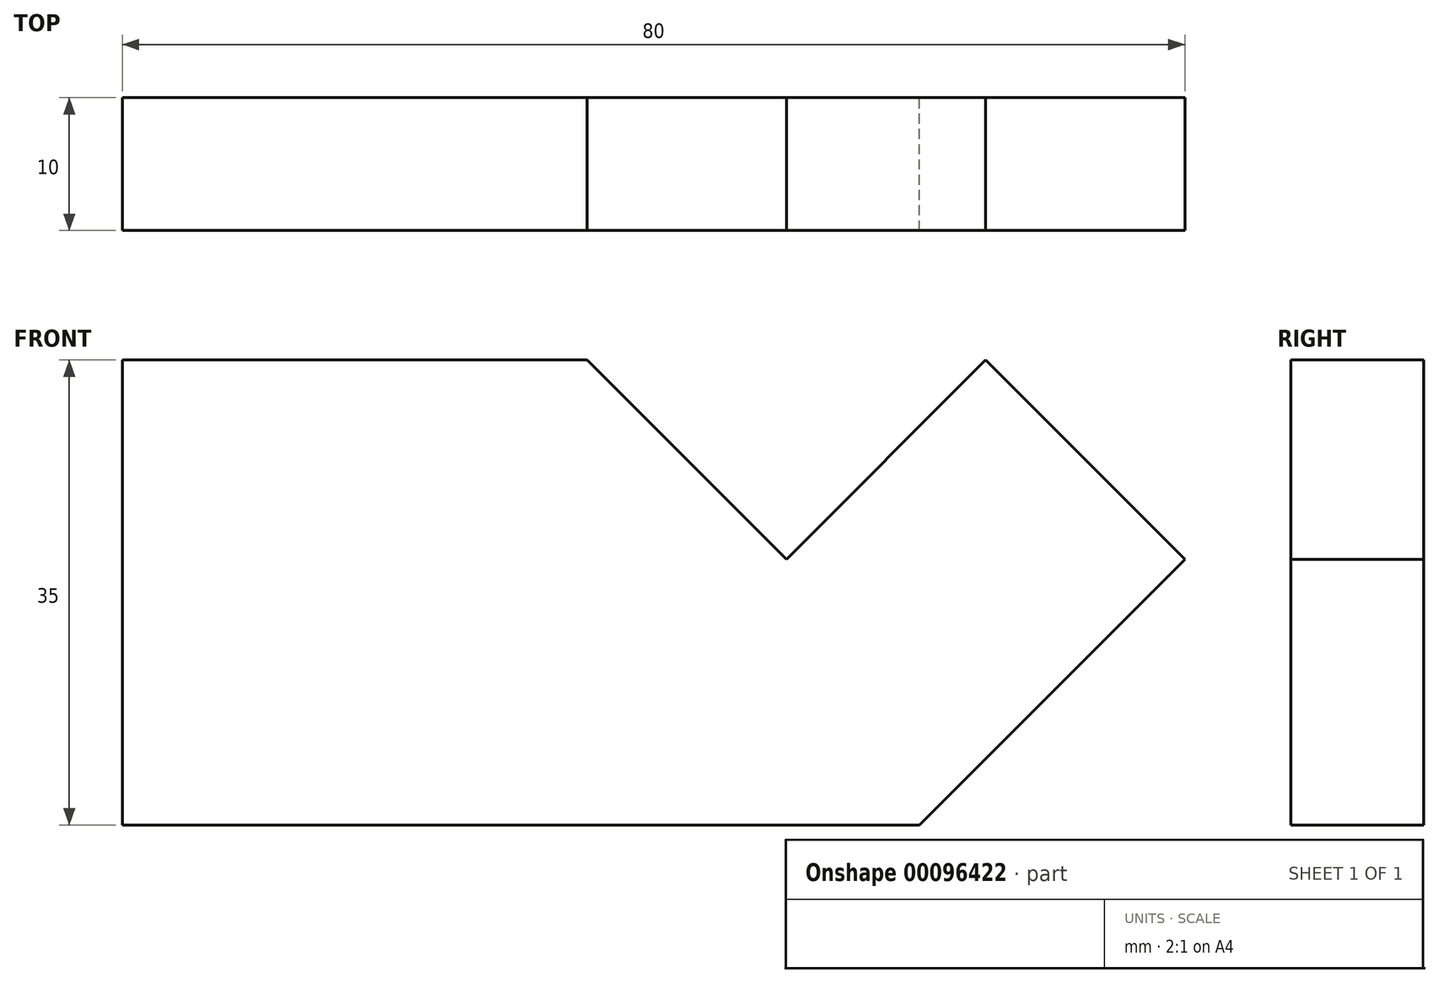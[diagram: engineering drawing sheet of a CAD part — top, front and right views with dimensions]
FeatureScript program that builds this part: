
annotation { "Feature Type Name" : "Feature", "Feature Type Description" : "" }
export const myFeature = defineFeature(function(context is Context, id is Id, definition is map)
    precondition{}
    {
        {
            var Q0;
            Q0=qCreatedBy(makeId("Front.planeOp"),FACE);
            var sketch = newSketch(context, id + "F0", { "sketchPlane" : qUnion([Q0])});
            skLineSegment(sketch, "E0.bottom", {"start": v(0, 0) * mm, "end": v(80, 0) * mm, "construction": true});
            skLineSegment(sketch, "E0.top", {"start": v(0, 35) * mm, "end": v(80, 35) * mm, "construction": true});
            skLineSegment(sketch, "E0.left", {"start": v(0, 0) * mm, "end": v(0, 35) * mm, "construction": true});
            skLineSegment(sketch, "E0.right", {"start": v(80, 0) * mm, "end": v(80, 35) * mm, "construction": true});
            skLineSegment(sketch, "E1", {"start": v(0, 0) * mm, "end": v(0, 35) * mm});
            skLineSegment(sketch, "E2", {"start": v(35, 35) * mm, "end": v(50, 20) * mm});
            skLineSegment(sketch, "E3", {"start": v(50, 20) * mm, "end": v(65, 35) * mm});
            skLineSegment(sketch, "E4", {"start": v(65, 35) * mm, "end": v(80, 20) * mm});
            skLineSegment(sketch, "E5", {"start": v(80, 20) * mm, "end": v(60, 0) * mm});
            skLineSegment(sketch, "E6", {"start": v(60, 0) * mm, "end": v(0, 0) * mm});
            skLineSegment(sketch, "E7", {"start": v(0, 35) * mm, "end": v(35, 35) * mm});
            skSolve(sketch);
        }
        {
            var Q0;
            Q0 = qSketchRegion(id + "F0", true);
            extrude(context, id + "F1", {"entities" : qUnion([Q0]), "endBound" : BoundingType.SYMMETRIC, "depth" : 10 * mm});
        }
    });
